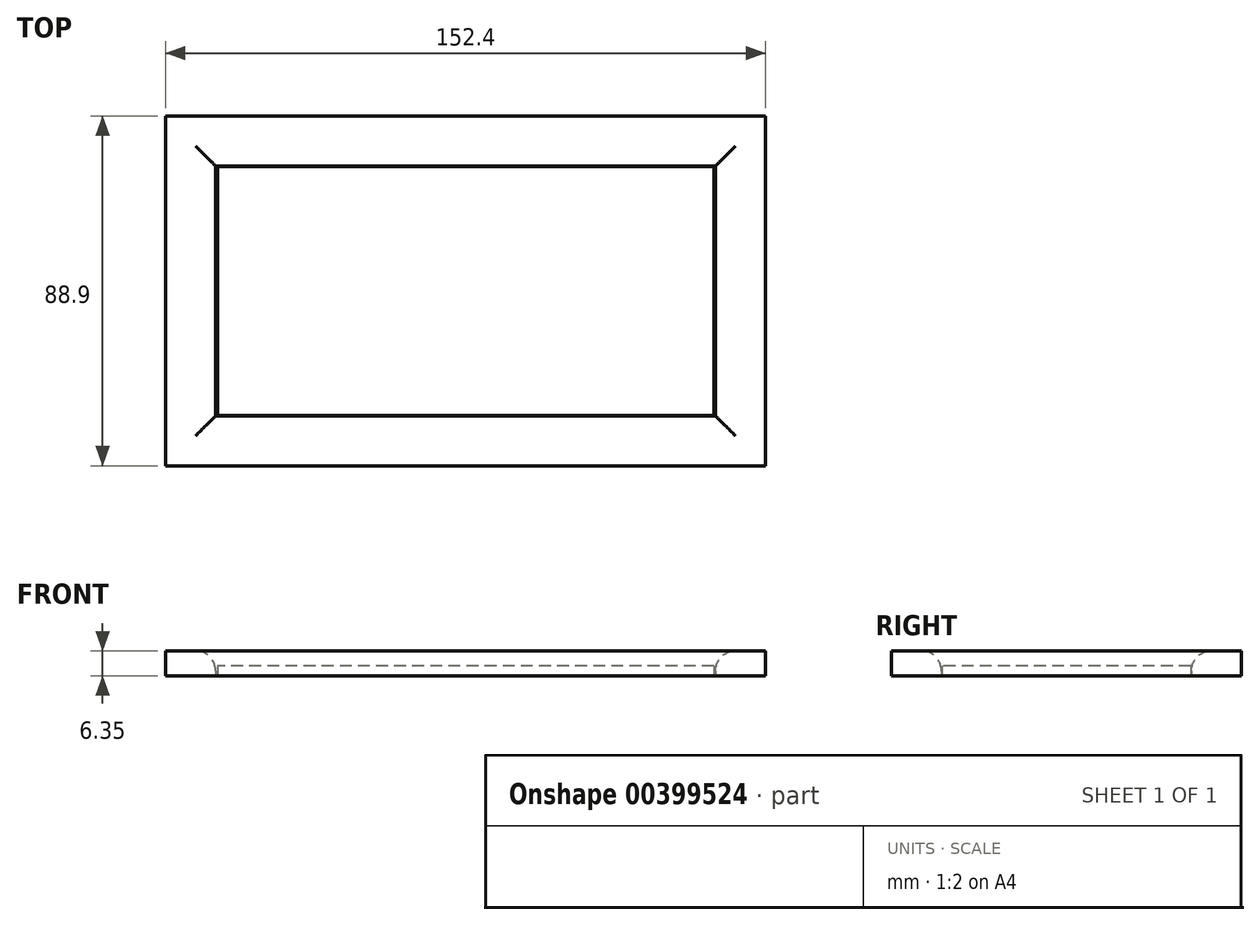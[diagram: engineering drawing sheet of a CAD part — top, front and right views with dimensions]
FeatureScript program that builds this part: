
annotation { "Feature Type Name" : "Feature", "Feature Type Description" : "" }
export const myFeature = defineFeature(function(context is Context, id is Id, definition is map)
    precondition{}
    {
        {
            var Q0;
            Q0=qCreatedBy(makeId("Top.planeOp"),FACE);
            var sketch = newSketch(context, id + "F0", { "sketchPlane" : qUnion([Q0])});
            skLineSegment(sketch, "E0.bottom", {"start": v(-76.2, -44.45) * mm, "end": v(76.2, -44.45) * mm});
            skLineSegment(sketch, "E0.top", {"start": v(-76.2, 44.45) * mm, "end": v(76.2, 44.45) * mm});
            skLineSegment(sketch, "E0.left", {"start": v(-76.2, -44.45) * mm, "end": v(-76.2, 44.45) * mm});
            skLineSegment(sketch, "E0.right", {"start": v(76.2, -44.45) * mm, "end": v(76.2, 44.45) * mm});
            skPoint(sketch, "E0.middle", {"position": v(0, 0) * mm});
            skLineSegment(sketch, "E1", {"start": v(-63.5, 44.45) * mm, "end": v(-63.5, -44.45) * mm});
            skLineSegment(sketch, "E2", {"start": v(76.2, -31.75) * mm, "end": v(-76.2, -31.75) * mm});
            skLineSegment(sketch, "E3", {"start": v(63.5, -44.4) * mm, "end": v(63.5, 44.45) * mm});
            skLineSegment(sketch, "E4", {"start": v(63.5, 44.45) * mm, "end": v(63.5, 44.45) * mm});
            skLineSegment(sketch, "E5", {"start": v(76.2, 31.75) * mm, "end": v(-76.2, 31.75) * mm});
            skSolve(sketch);
        }
        {
            var Q0;
            {var subQ0=sQuery(id+"F0.wireOp",EDGE,"E0.left");var subQ1=sQuery(id+"F0.wireOp",EDGE,"E0.bottom");var subQ2=makeQuery(id+"F0.imprint","INTERSECT",VERTEX,{"derivedFrom":[subQ1,subQ0]});Q0=makeQuery(id+"F0.imprint","IMPRINT",FACE,{"disambiguationData":[TD([[makeQuery(id+"F0.imprint","IMPRINT",EDGE,{"disambiguationData":[TD([[subQ2,-1.0]])],"derivedFrom":subQ1}),1.0]])]});}
            var Q1;
            {var subQ1=sQuery(id+"F0.wireOp",EDGE,"E0.right");var subQ5=sQuery(id+"F0.wireOp",EDGE,"E0.bottom");var subQ8=makeQuery(id+"F0.imprint","INTERSECT",VERTEX,{"derivedFrom":[subQ5,subQ1]});Q1=makeQuery(id+"F0.imprint","IMPRINT",FACE,{"disambiguationData":[TD([[makeQuery(id+"F0.imprint","IMPRINT",EDGE,{"disambiguationData":[TD([[subQ8,1.0]])],"derivedFrom":subQ5}),1.0]])]});}
            var Q2;
            {var subQ0=sQuery(id+"F0.wireOp",EDGE,"E2");var subQ1=sQuery(id+"F0.wireOp",EDGE,"E0.left");var subQ2=makeQuery(id+"F0.imprint","INTERSECT",VERTEX,{"derivedFrom":[subQ1,subQ0]});Q2=makeQuery(id+"F0.imprint","IMPRINT",FACE,{"disambiguationData":[TD([[makeQuery(id+"F0.imprint","IMPRINT",EDGE,{"disambiguationData":[TD([[subQ2,-1.0]])],"derivedFrom":subQ1}),-1.0]])]});}
            var Q3;
            {var subQ0=sQuery(id+"F0.wireOp",EDGE,"E2");var subQ1=sQuery(id+"F0.wireOp",EDGE,"E0.right");var subQ2=makeQuery(id+"F0.imprint","INTERSECT",VERTEX,{"derivedFrom":[subQ1,subQ0]});Q3=makeQuery(id+"F0.imprint","IMPRINT",FACE,{"disambiguationData":[TD([[makeQuery(id+"F0.imprint","IMPRINT",EDGE,{"disambiguationData":[TD([[subQ2,-1.0]])],"derivedFrom":subQ1}),1.0]])]});}
            var Q4;
            {var subQ0=sQuery(id+"F0.wireOp",EDGE,"E0.left");var subQ1=sQuery(id+"F0.wireOp",EDGE,"E0.top");var subQ2=makeQuery(id+"F0.imprint","INTERSECT",VERTEX,{"derivedFrom":[subQ1,subQ0]});Q4=makeQuery(id+"F0.imprint","IMPRINT",FACE,{"disambiguationData":[TD([[makeQuery(id+"F0.imprint","IMPRINT",EDGE,{"disambiguationData":[TD([[subQ2,-1.0]])],"derivedFrom":subQ1}),-1.0]])]});}
            var Q5;
            {var subQ0=sQuery(id+"F0.wireOp",EDGE,"E1");var subQ1=sQuery(id+"F0.wireOp",EDGE,"E0.top");var subQ2=makeQuery(id+"F0.imprint","INTERSECT",VERTEX,{"derivedFrom":[subQ1,subQ0]});Q5=makeQuery(id+"F0.imprint","IMPRINT",FACE,{"disambiguationData":[TD([[makeQuery(id+"F0.imprint","IMPRINT",EDGE,{"disambiguationData":[TD([[subQ2,-1.0]])],"derivedFrom":subQ1}),-1.0]])]});}
            var Q6;
            {var subQ0=sQuery(id+"F0.wireOp",EDGE,"E0.right");var subQ1=sQuery(id+"F0.wireOp",EDGE,"E0.top");var subQ2=makeQuery(id+"F0.imprint","INTERSECT",VERTEX,{"derivedFrom":[subQ1,subQ0]});Q6=makeQuery(id+"F0.imprint","IMPRINT",FACE,{"disambiguationData":[TD([[makeQuery(id+"F0.imprint","IMPRINT",EDGE,{"disambiguationData":[TD([[subQ2,1.0]])],"derivedFrom":subQ1}),-1.0]])]});}
            extrude(context, id + "F1", {"entities" : qUnion([Q0, Q1, Q2, Q3, Q4, Q5, Q6]), "depth" : 6.35 * mm});
        }
        {
            var Q0;
            Q0=qCreatedBy(makeId("Top.planeOp"),FACE);
            var sketch = newSketch(context, id + "F2", { "sketchPlane" : qUnion([Q0])});
            skLineSegment(sketch, "E6.bottom", {"start": v(63.06, 31.6) * mm, "end": v(-63.06, 31.6) * mm});
            skLineSegment(sketch, "E6.top", {"start": v(63.06, -31.6) * mm, "end": v(-63.06, -31.6) * mm});
            skLineSegment(sketch, "E6.left", {"start": v(63.06, 31.6) * mm, "end": v(63.06, -31.6) * mm});
            skLineSegment(sketch, "E6.right", {"start": v(-63.06, 31.6) * mm, "end": v(-63.06, -31.6) * mm});
            skPoint(sketch, "E6.middle", {"position": v(0, 0) * mm});
            skSolve(sketch);
        }
        {
            var Q0;
            Q0=makeQuery(id+"F2.imprint","IMPRINT",FACE,{"disambiguationData":[TD([[makeQuery(id+"F2.imprint","IMPRINT",EDGE,{"derivedFrom":sQuery(id+"F2.wireOp",EDGE,"E6.bottom")}),1.0]])]});
            extrude(context, id + "F3", {"entities" : qUnion([Q0]), "depth" : 2.54 * mm});
        }
        {
            var Q0;
            Q0=makeQuery(id+"F1.opExtrude","CAP_EDGE",EDGE,{"disambiguationData":[OSD([sQuery(id+"F0.wireOp",EDGE,"E5")])],"isStart":false});
            fillet(context, id + "F4", {"entities" : qUnion([Q0]), "radius" : 5.08 * mm, "tangentPropagation" : true, "allowEdgeOverflow" : false});
        }
        {
            var Q0;
            Q0=makeQuery(id+"F1.opExtrude","CAP_EDGE",EDGE,{"disambiguationData":[OSD([sQuery(id+"F0.wireOp",EDGE,"E3")])],"isStart":false});
            fillet(context, id + "F5", {"entities" : qUnion([Q0]), "radius" : 5.08 * mm, "tangentPropagation" : true, "allowEdgeOverflow" : false});
        }
        {
            var Q0;
            Q0=makeQuery(id+"F1.opExtrude","CAP_EDGE",EDGE,{"disambiguationData":[OSD([sQuery(id+"F0.wireOp",EDGE,"E2")])],"isStart":false});
            fillet(context, id + "F6", {"entities" : qUnion([Q0]), "radius" : 5.08 * mm, "tangentPropagation" : true, "allowEdgeOverflow" : false});
        }
        {
            var Q0;
            Q0=makeQuery(id+"F1.opExtrude","CAP_EDGE",EDGE,{"disambiguationData":[OSD([sQuery(id+"F0.wireOp",EDGE,"E1")])],"isStart":false});
            fillet(context, id + "F7", {"entities" : qUnion([Q0]), "radius" : 5.08 * mm, "tangentPropagation" : true, "allowEdgeOverflow" : false});
        }
    });
